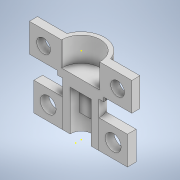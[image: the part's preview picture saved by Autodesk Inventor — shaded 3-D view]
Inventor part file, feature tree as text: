
AUTODESK INVENTOR PART (.ipt)
format: ipt  version: 2020.2 (Build 242310000, 310)  size: 287,232 bytes
history: native  units: in
note: dims shown in document units (in); Inventor stores cm internally (conversion verified against a paired STEP export)
features: sketch x16, extrude x11, plane x3, projected_geometry x3, hole x2
ambient origin geometry x8: Origin, YZ Plane, XZ Plane, XY Plane, X Axis, Y Axis, Z Axis, Center Point
bodies: Body1 (feature_tree)
feature tree (35):
  extrude  "Extrusion2"  Depth=0.3543in
  extrude  "Extrusion3"  Depth=0.0394in
  extrude  "Extrusion4"  Depth=0.0394in TaperAngle=0.0deg
  sketch  "Sketch11"  dims[d20=0.0394in d59=0.3689in]
  sketch  "Sketch12"  dims[d60=0.4476in d61=0.0787in d62=0.0in]
  extrude  "Extrusion11"  Depth=0.0394in
  extrude  "Extrusion12"  Depth=0.0787in TaperAngle=0.0deg
  sketch  "Sketch14"  dims[d63=0.315in d64=0.0in d72=0.0039in]
  sketch  "Sketch15"  dims[d73=0.2756in d74=0.2756in]
  plane  "Work Plane3"
  sketch  "Sketch17"  dims[d81=0.1378in d82=0.1378in]
  plane  "Work Plane2"
  extrude  "Extrusion17"  Depth=0.315in
  plane  "Work Plane1"
  extrude  "Extrusion18"  Depth=0.2756in
  extrude  "Extrusion20"  Depth=0.1378in
  hole  "Hole2"  [1 undecoded]
  sketch  "Sketch22"  dims[d99=0.0787in d100=0.0in d101=0.0787in d102=0.0in]
  sketch  "Sketch23"  dims[d104=3.0in d105=0.0in d106=0.2756in d107=0.0in]
  hole  "Hole3"  [1 undecoded]
  extrude  "Extrusion19"  Depth=0.154in
  extrude  "Extrusion21"  Depth=0.0787in TaperAngle=0.0deg
  extrude  "Extrusion22"  Depth=0.2756in TaperAngle=0.0deg
  sketch  "Sketch3"  dims[d10=0.3543in d11=0.2047in]
  sketch  "Sketch4"  dims[d12=0.1575in d13=0.0in d14=0.0394in]
  projected_geometry  "Projected Loop1"
  sketch  "Sketch5"  dims[d16=0.2362in d17=0.0in d18=0.0394in d19=0.0in]
  sketch  "Sketch19"  dims[d93=0.2756in d94=0.2756in]
  sketch  "Sketch20"  dims[d95=0.2756in d96=0.2756in]
  sketch  "Sketch21"  dims[d97=0.154in d98=0.154in]
  sketch  "Sketch24"  dims[d108=0.1339in d109=0.75in d110=0.248in d111=0.25in d112=90.0deg d113=1.0in d114=0.8108in]
  sketch  "Sketch25"  dims[d115=0.1339in d116=0.75in d117=0.248in d118=0.25in d119=90.0deg d120=1.0in d121=0.8108in]
  sketch  "Sketch26"  dims[d122=0.0787in d123=0.0in d124=1.0in d125=0.0in]
  projected_geometry  "Projected Loop3"
  projected_geometry  "Projected Loop4"
note: 2 required parameter values undecoded (feature->parameter linkage not recoverable at this tier; creation-order binding heuristic only, values carry confidence <= 0.55)
